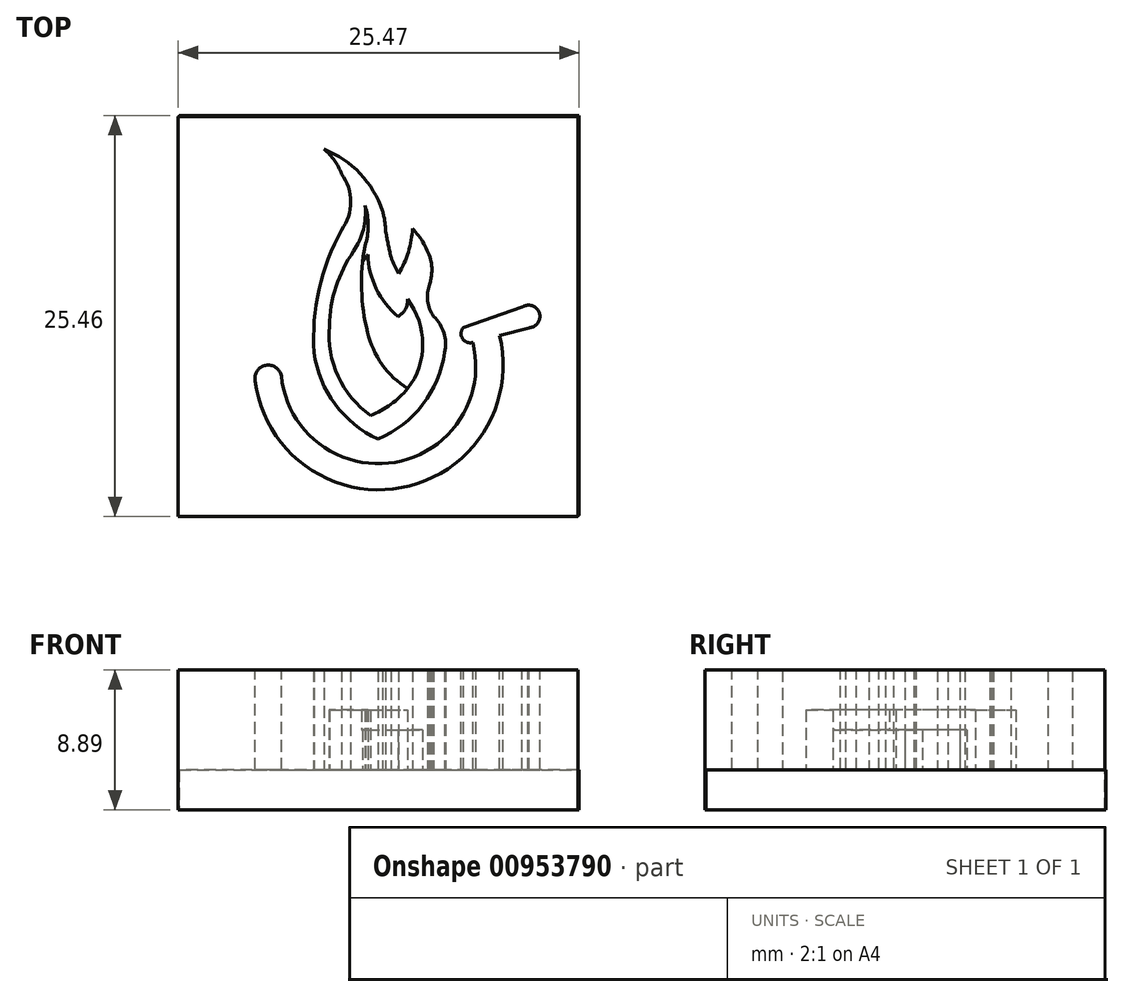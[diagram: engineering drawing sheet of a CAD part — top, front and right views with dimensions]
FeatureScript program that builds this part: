
annotation { "Feature Type Name" : "Feature", "Feature Type Description" : "" }
export const myFeature = defineFeature(function(context is Context, id is Id, definition is map)
    precondition{}
    {
        {
            var Q0;
            Q0=qCreatedBy(makeId("Top.planeOp"),FACE);
            var sketch = newSketch(context, id + "F0", { "sketchPlane" : qUnion([Q0])});
            skLineSegment(sketch, "E0.bottom", {"start": v(12.7, 12.7) * mm, "end": v(-12.7, 12.7) * mm});
            skLineSegment(sketch, "E0.top", {"start": v(12.7, -12.7) * mm, "end": v(-12.7, -12.7) * mm});
            skLineSegment(sketch, "E0.left", {"start": v(12.7, 12.7) * mm, "end": v(12.7, -12.7) * mm});
            skLineSegment(sketch, "E0.right", {"start": v(-12.7, 12.7) * mm, "end": v(-12.7, -12.7) * mm});
            skPoint(sketch, "E0.middle", {"position": v(0, 0) * mm});
            skLineSegment(sketch, "E1", {"start": v(0, 12.7) * mm, "end": v(0, -12.7) * mm, "construction": true});
            skArc(sketch, "E2", {"start": v(-2.32, 9.06) * mm, "mid": v(-2.77, 9.91) * mm, "end": v(-3.43, 10.62) * mm});
            skArc(sketch, "E3", {"start": v(3.37, 3.48) * mm, "mid": v(2.91, 4.61) * mm, "end": v(2.18, 5.6) * mm});
            skArc(sketch, "E4", {"start": v(-2.32, 5.5) * mm, "mid": v(-1.75, 7.28) * mm, "end": v(-2.32, 9.06) * mm});
            skArc(sketch, "E5", {"start": v(0.28, 6.7) * mm, "mid": v(-1.14, 9.07) * mm, "end": v(-3.43, 10.62) * mm});
            skArc(sketch, "E6", {"start": v(-2.32, 5.5) * mm, "mid": v(-3.76, 1.72) * mm, "end": v(-4.07, -2.3) * mm});
            skArc(sketch, "E7", {"start": v(-4.07, -2.3) * mm, "mid": v(-2.74, -5.57) * mm, "end": v(0, -7.78) * mm});
            skArc(sketch, "E8", {"start": v(0, -7.78) * mm, "mid": v(2.83, -5.58) * mm, "end": v(4.23, -2.28) * mm});
            skArc(sketch, "E9", {"start": v(3.27, 2.04) * mm, "mid": v(3.14, 0.99) * mm, "end": v(3.53, 0) * mm});
            skArc(sketch, "E10", {"start": v(4.23, -2.28) * mm, "mid": v(4.17, -1.05) * mm, "end": v(3.53, 0) * mm});
            skArc(sketch, "E11", {"start": v(0.81, 3.78) * mm, "mid": v(1.04, 3.24) * mm, "end": v(1.3, 2.72) * mm});
            skArc(sketch, "E12", {"start": v(1.3, 2.72) * mm, "mid": v(1.92, 4.1) * mm, "end": v(2.18, 5.6) * mm});
            skArc(sketch, "E13", {"start": v(-0.66, 3.94) * mm, "mid": v(-2.13, -1.18) * mm, "end": v(0.2, -5.97) * mm});
            skArc(sketch, "E14", {"start": v(-0.66, 3.94) * mm, "mid": v(-0.12, 1.77) * mm, "end": v(1.26, 0) * mm});
            skArc(sketch, "E15", {"start": v(1.26, 0) * mm, "mid": v(1.73, 0.46) * mm, "end": v(1.87, 1.1) * mm});
            skArc(sketch, "E16", {"start": v(0.2, -5.97) * mm, "mid": v(2.7, -2.83) * mm, "end": v(1.87, 1.1) * mm});
            skArc(sketch, "E17", {"start": v(0.49, 5.39) * mm, "mid": v(0.42, 6.05) * mm, "end": v(0.28, 6.7) * mm});
            skArc(sketch, "E18", {"start": v(0.49, 5.39) * mm, "mid": v(0.64, 4.58) * mm, "end": v(0.81, 3.78) * mm});
            skArc(sketch, "E19", {"start": v(3.27, 2.04) * mm, "mid": v(3.4, 2.75) * mm, "end": v(3.37, 3.48) * mm});
            skPoint(sketch, "E20.orphan", {"position": v(3.53, 2.53) * mm});
            skArc(sketch, "E21", {"start": v(-3.1, -0.6) * mm, "mid": v(-2.54, -3.8) * mm, "end": v(-0.48, -6.3) * mm});
            skArc(sketch, "E22", {"start": v(-1.56, 4.14) * mm, "mid": v(-2.68, 1.89) * mm, "end": v(-3.1, -0.6) * mm});
            skArc(sketch, "E23", {"start": v(-0.84, 4.48) * mm, "mid": v(-1.05, 1.72) * mm, "end": v(-0.67, -1) * mm});
            skArc(sketch, "E24", {"start": v(-0.67, -1) * mm, "mid": v(0.26, -3.05) * mm, "end": v(1.88, -4.59) * mm});
            skArc(sketch, "E25", {"start": v(-0.48, -6.3) * mm, "mid": v(0.8, -5.58) * mm, "end": v(1.88, -4.59) * mm});
            skArc(sketch, "E26", {"start": v(-1.56, 4.14) * mm, "mid": v(-0.94, 5.53) * mm, "end": v(-0.83, 7.05) * mm});
            skArc(sketch, "E27", {"start": v(-0.84, 4.48) * mm, "mid": v(-0.64, 5.76) * mm, "end": v(-0.83, 7.05) * mm});
            skPoint(sketch, "E28.orphan", {"position": v(-0.67, 5.22) * mm});
            skSolve(sketch);
        }
        {
            var Q0;
            Q0=makeQuery(id+"F0.imprint","IMPRINT",FACE,{"disambiguationData":[TD([[makeQuery(id+"F0.imprint","IMPRINT",EDGE,{"derivedFrom":sQuery(id+"F0.wireOp",EDGE,"E0.bottom")}),1.0]])]});
            var Q1;
            Q1=makeQuery(id+"F0.imprint","IMPRINT",FACE,{"disambiguationData":[TD([[makeQuery(id+"F0.imprint","IMPRINT",EDGE,{"derivedFrom":sQuery(id+"F0.wireOp",EDGE,"E13")}),1.0]])]});
            var Q2;
            {var subQ0=sQuery(id+"F0.wireOp",EDGE,"E21");Q2=makeQuery(id+"F0.imprint","IMPRINT",FACE,{"disambiguationData":[TD([[makeQuery(id+"F0.imprint","IMPRINT",EDGE,{"derivedFrom":subQ0}),1.0]])]});}
            extrude(context, id + "F1", {"entities" : qUnion([Q0, Q1, Q2]), "depth" : 3.8 * mm, "offsetDistance" : 25.4 * mm});
        }
        {
            var Q0;
            Q0=makeQuery(id+"F1.opExtrude","CAP_FACE",FACE,{"disambiguationData":[OSD([sQuery(id+"F0.wireOp",EDGE,"E0.bottom"),sQuery(id+"F0.wireOp",EDGE,"E0.top"),sQuery(id+"F0.wireOp",EDGE,"E0.left"),sQuery(id+"F0.wireOp",EDGE,"E0.right"),sQuery(id+"F0.wireOp",EDGE,"E2"),sQuery(id+"F0.wireOp",EDGE,"E3"),sQuery(id+"F0.wireOp",EDGE,"E4"),sQuery(id+"F0.wireOp",EDGE,"E5"),sQuery(id+"F0.wireOp",EDGE,"E6"),sQuery(id+"F0.wireOp",EDGE,"E7"),sQuery(id+"F0.wireOp",EDGE,"E8"),sQuery(id+"F0.wireOp",EDGE,"E9"),sQuery(id+"F0.wireOp",EDGE,"E10"),sQuery(id+"F0.wireOp",EDGE,"E11"),sQuery(id+"F0.wireOp",EDGE,"E12"),sQuery(id+"F0.wireOp",EDGE,"E17"),sQuery(id+"F0.wireOp",EDGE,"E18"),sQuery(id+"F0.wireOp",EDGE,"E19")])],"isStart":false});
            var sketch = newSketch(context, id + "F2", { "sketchPlane" : qUnion([Q0])});
            skPoint(sketch, "E29.endSnap0", {"position": v(12.7, 0) * mm});
            skArc(sketch, "E30", {"start": v(-7.8, -4.1) * mm, "mid": v(2, -10.76) * mm, "end": v(7.39, -0.2) * mm});
            skArc(sketch, "E31", {"start": v(-6.15, -3.76) * mm, "mid": v(1.36, -9.2) * mm, "end": v(5.85, -1.1) * mm});
            skArc(sketch, "E32", {"start": v(-6.15, -3.76) * mm, "mid": v(-7.14, -3.1) * mm, "end": v(-7.8, -4.1) * mm});
            skArc(sketch, "E33", {"start": v(7.39, -0.2) * mm, "mid": v(6.5, -0.45) * mm, "end": v(5.85, -1.1) * mm});
            skSolve(sketch);
        }
        {
            var Q0;
            Q0 = qSketchRegion(id + "F2", true);
            extrude(context, id + "F3", {"entities" : qUnion([Q0]), "operationType" : NewBodyOperationType.REMOVE, "oppositeDirection" : true, "depth" : 6.35 * mm, "offsetDistance" : 25.4 * mm});
        }
        {
            var Q0;
            Q0=qCreatedBy(makeId("Top.planeOp"),FACE);
            var sketch = newSketch(context, id + "F4", { "sketchPlane" : qUnion([Q0])});
            skLineSegment(sketch, "E34.bottom", {"start": v(-12.63, 12.76) * mm, "end": v(12.77, 12.76) * mm});
            skLineSegment(sketch, "E34.top", {"start": v(-12.63, -12.64) * mm, "end": v(12.77, -12.64) * mm});
            skLineSegment(sketch, "E34.left", {"start": v(-12.63, 12.76) * mm, "end": v(-12.63, -12.64) * mm});
            skLineSegment(sketch, "E34.right", {"start": v(12.77, 12.76) * mm, "end": v(12.77, -12.64) * mm});
            skSolve(sketch);
        }
        {
            var Q0;
            Q0 = qSketchRegion(id + "F4", true);
            var Q1;
            Q1=makeQuery(id+"F1.opExtrude","CAP_FACE",FACE,{"disambiguationData":[OSD([sQuery(id+"F0.wireOp",EDGE,"E0.bottom"),sQuery(id+"F0.wireOp",EDGE,"E0.top"),sQuery(id+"F0.wireOp",EDGE,"E0.left"),sQuery(id+"F0.wireOp",EDGE,"E0.right"),sQuery(id+"F0.wireOp",EDGE,"E2"),sQuery(id+"F0.wireOp",EDGE,"E3"),sQuery(id+"F0.wireOp",EDGE,"E4"),sQuery(id+"F0.wireOp",EDGE,"E5"),sQuery(id+"F0.wireOp",EDGE,"E6"),sQuery(id+"F0.wireOp",EDGE,"E7"),sQuery(id+"F0.wireOp",EDGE,"E8"),sQuery(id+"F0.wireOp",EDGE,"E9"),sQuery(id+"F0.wireOp",EDGE,"E10"),sQuery(id+"F0.wireOp",EDGE,"E11"),sQuery(id+"F0.wireOp",EDGE,"E12"),sQuery(id+"F0.wireOp",EDGE,"E17"),sQuery(id+"F0.wireOp",EDGE,"E18"),sQuery(id+"F0.wireOp",EDGE,"E19")])],"isStart":false});
            extrude(context, id + "F5", {"entities" : qUnion([Q0, Q1]), "operationType" : NewBodyOperationType.ADD, "depth" : 2.54 * mm, "offsetDistance" : 25.4 * mm});
        }
        {
            var Q0;
            Q0=makeQuery(id+"F5.opExtrude","CAP_FACE",FACE,{"disambiguationData":[OSD([sQuery(id+"F0.wireOp",EDGE,"E0.bottom"),sQuery(id+"F0.wireOp",EDGE,"E0.top"),sQuery(id+"F0.wireOp",EDGE,"E0.left"),sQuery(id+"F0.wireOp",EDGE,"E0.right"),sQuery(id+"F0.wireOp",EDGE,"E2"),sQuery(id+"F0.wireOp",EDGE,"E3"),sQuery(id+"F0.wireOp",EDGE,"E4"),sQuery(id+"F0.wireOp",EDGE,"E5"),sQuery(id+"F0.wireOp",EDGE,"E6"),sQuery(id+"F0.wireOp",EDGE,"E7"),sQuery(id+"F0.wireOp",EDGE,"E8"),sQuery(id+"F0.wireOp",EDGE,"E9"),sQuery(id+"F0.wireOp",EDGE,"E10"),sQuery(id+"F0.wireOp",EDGE,"E11"),sQuery(id+"F0.wireOp",EDGE,"E12"),sQuery(id+"F0.wireOp",EDGE,"E17"),sQuery(id+"F0.wireOp",EDGE,"E18"),sQuery(id+"F0.wireOp",EDGE,"E19")])],"isStart":false});
            var sketch = newSketch(context, id + "F6", { "sketchPlane" : qUnion([Q0])});
            skLineSegment(sketch, "E35", {"start": v(5.42, -0.7) * mm, "end": v(9.14, 0.59) * mm});
            skLineSegment(sketch, "E36", {"start": v(9.55, 0.73) * mm, "end": v(9.55, 0.72) * mm});
            skArc(sketch, "E37", {"start": v(9.57, -0.72) * mm, "mid": v(10.24, 0.23) * mm, "end": v(9.14, 0.59) * mm});
            skLineSegment(sketch, "E38", {"start": v(9.57, -0.72) * mm, "end": v(6, -1.65) * mm});
            skLineSegment(sketch, "E39.trimOffspring", {"start": v(9.52, 0.72) * mm, "end": v(9.55, 0.73) * mm});
            skArc(sketch, "E40", {"start": v(5.42, -0.7) * mm, "mid": v(5.35, -1.4) * mm, "end": v(6, -1.65) * mm});
            skSolve(sketch);
        }
        {
            var Q0;
            {var subQ5=sQuery(id+"F6.wireOp",EDGE,"E36");Q0=makeQuery(id+"F6.imprint","IMPRINT",FACE,{"disambiguationData":[TD([[makeQuery(id+"F6.imprint","IMPRINT",EDGE,{"derivedFrom":subQ5}),-1.0]])]});}
            var Q1;
            {var subQ0=sQuery(id+"F6.wireOp",EDGE,"LpHUefbm-SuxV-FGb6-HNIV-Q6mAyEG2d9lf");var subQ1=sQuery(id+"F6.wireOp",EDGE,"E35");var subQ2=makeQuery(id+"F6.imprint","INTERSECT",VERTEX,{"derivedFrom":[subQ1,subQ0]});Q1=makeQuery(id+"F6.imprint","IMPRINT",FACE,{"disambiguationData":[TD([[makeQuery(id+"F6.imprint","IMPRINT",EDGE,{"disambiguationData":[TD([[subQ2,-1.0]])],"derivedFrom":subQ1}),-1.0]])]});}
            var Q2;
            {var subQ5=makeQuery(id+"F5.opExtrude","CAP_EDGE",EDGE,{"disambiguationData":[OSD([sQuery(id+"F2.wireOp",EDGE,"E33")])],"isStart":false});Q2=makeQuery(id+"F6.imprint","IMPRINT",FACE,{"disambiguationData":[TD([[makeQuery(id+"F6.imprint","IMPRINT",EDGE,{"derivedFrom":subQ5}),-1.0]])]});}
            extrude(context, id + "F7", {"entities" : qUnion([Q0, Q1, Q2]), "operationType" : NewBodyOperationType.REMOVE, "oppositeDirection" : true, "depth" : 3.8 * mm, "offsetDistance" : 25.4 * mm});
        }
        {
            var Q0;
            {var subQ1=sQuery(id+"F0.wireOp",EDGE,"E14");Q0=makeQuery(id+"F0.imprint","IMPRINT",FACE,{"disambiguationData":[TD([[makeQuery(id+"F0.imprint","IMPRINT",EDGE,{"derivedFrom":subQ1}),-1.0]])]});}
            var Q1;
            Q1=makeQuery(id+"F5.opExtrude","CAP_FACE",FACE,{"disambiguationData":[OSD([sQuery(id+"F0.wireOp",EDGE,"E0.bottom"),sQuery(id+"F0.wireOp",EDGE,"E0.top"),sQuery(id+"F0.wireOp",EDGE,"E0.left"),sQuery(id+"F0.wireOp",EDGE,"E0.right"),sQuery(id+"F0.wireOp",EDGE,"E2"),sQuery(id+"F0.wireOp",EDGE,"E3"),sQuery(id+"F0.wireOp",EDGE,"E4"),sQuery(id+"F0.wireOp",EDGE,"E5"),sQuery(id+"F0.wireOp",EDGE,"E6"),sQuery(id+"F0.wireOp",EDGE,"E7"),sQuery(id+"F0.wireOp",EDGE,"E8"),sQuery(id+"F0.wireOp",EDGE,"E9"),sQuery(id+"F0.wireOp",EDGE,"E10"),sQuery(id+"F0.wireOp",EDGE,"E11"),sQuery(id+"F0.wireOp",EDGE,"E12"),sQuery(id+"F0.wireOp",EDGE,"E17"),sQuery(id+"F0.wireOp",EDGE,"E18"),sQuery(id+"F0.wireOp",EDGE,"E19")])],"isStart":false});
            extrude(context, id + "F8", {"entities" : qUnion([Q0, Q1]), "operationType" : NewBodyOperationType.ADD, "depth" : 2.54 * mm, "offsetDistance" : 25.4 * mm});
        }
        {
            var Q0;
            Q0=makeQuery(id+"F0.imprint","IMPRINT",FACE,{"disambiguationData":[TD([[makeQuery(id+"F0.imprint","IMPRINT",EDGE,{"derivedFrom":sQuery(id+"F0.wireOp",EDGE,"E21")}),1.0]])]});
            var Q1;
            {var subQ0=sQuery(id+"F0.wireOp",EDGE,"E16");var subQ1=sQuery(id+"F0.wireOp",EDGE,"E13");var subQ2=makeQuery(id+"F0.imprint","INTERSECT",VERTEX,{"derivedFrom":[subQ1,subQ0]});Q1=makeQuery(id+"F0.imprint","IMPRINT",FACE,{"disambiguationData":[TD([[makeQuery(id+"F0.imprint","IMPRINT",EDGE,{"disambiguationData":[TD([[subQ2,1.0]])],"derivedFrom":subQ1}),1.0]])]});}
            extrude(context, id + "F9", {"entities" : qUnion([Q0, Q1]), "operationType" : NewBodyOperationType.ADD, "depth" : 6.35 * mm, "offsetDistance" : 25.4 * mm});
        }
        {
            var Q0;
            {var subQ1=sQuery(id+"F0.wireOp",EDGE,"E14");Q0=makeQuery(id+"F0.imprint","IMPRINT",FACE,{"disambiguationData":[TD([[makeQuery(id+"F0.imprint","IMPRINT",EDGE,{"derivedFrom":subQ1}),-1.0]])]});}
            extrude(context, id + "F10", {"entities" : qUnion([Q0]), "operationType" : NewBodyOperationType.ADD, "depth" : 5.08 * mm, "offsetDistance" : 25.4 * mm});
        }
    });
